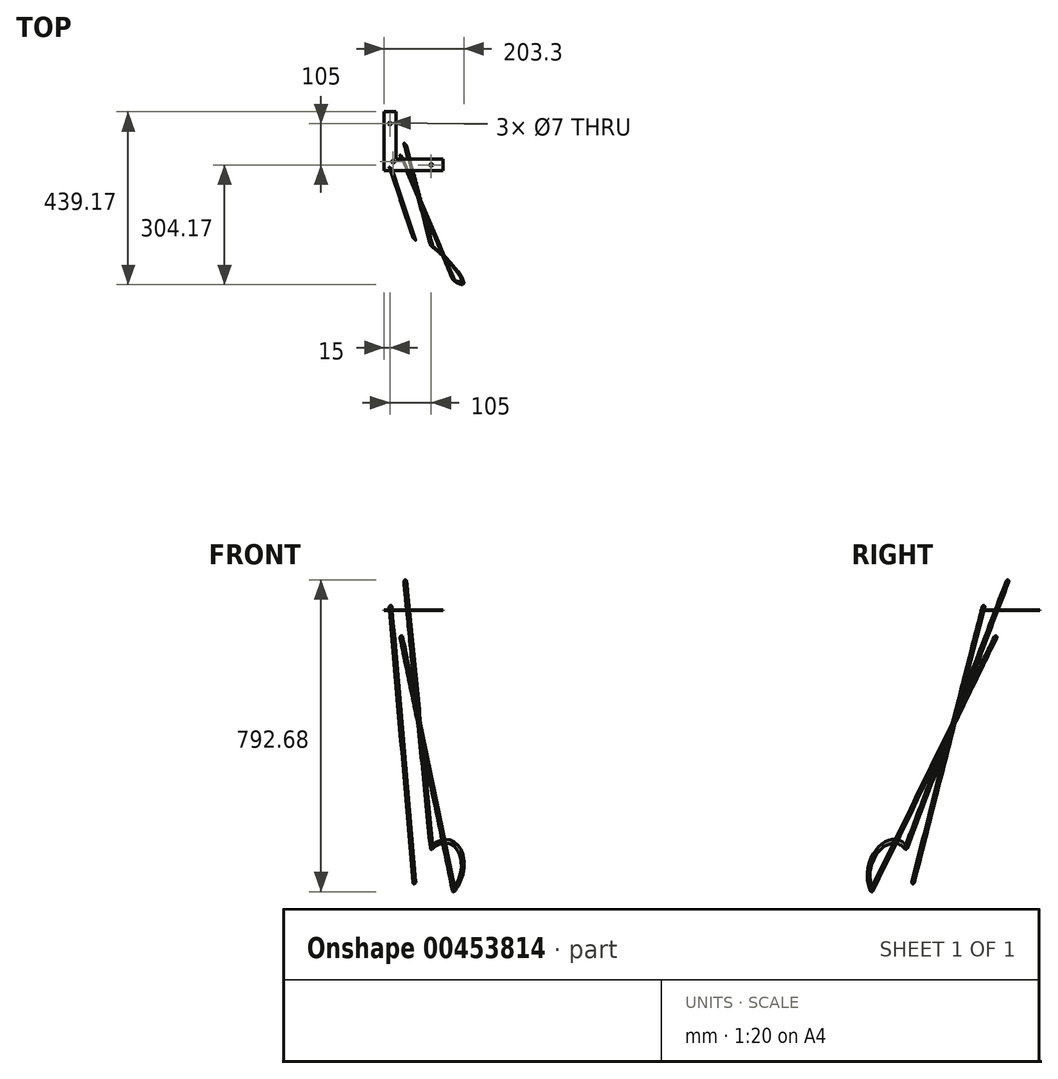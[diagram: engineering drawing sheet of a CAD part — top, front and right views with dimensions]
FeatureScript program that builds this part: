
annotation { "Feature Type Name" : "Feature", "Feature Type Description" : "" }
export const myFeature = defineFeature(function(context is Context, id is Id, definition is map)
    precondition{}
    {
        {
            var Q0;
            Q0=qCreatedBy(makeId("Top.planeOp"),FACE);
            var sketch = newSketch(context, id + "F0", { "sketchPlane" : qUnion([Q0])});
            skLineSegment(sketch, "E0", {"start": v(0, 0) * mm, "end": v(0, 150) * mm});
            skLineSegment(sketch, "E1", {"start": v(0, 150) * mm, "end": v(30, 150) * mm});
            skLineSegment(sketch, "E2", {"start": v(30, 150) * mm, "end": v(30, 30) * mm});
            skLineSegment(sketch, "E3", {"start": v(30, 30) * mm, "end": v(150, 30) * mm});
            skLineSegment(sketch, "E4", {"start": v(150, 30) * mm, "end": v(150, 0) * mm});
            skLineSegment(sketch, "E5", {"start": v(150, 0) * mm, "end": v(0, 0) * mm});
            skLineSegment(sketch, "E6", {"start": v(0, 150) * mm, "end": v(10, 150) * mm});
            skLineSegment(sketch, "E7", {"start": v(10, 150) * mm, "end": v(10, -10.8) * mm, "construction": true});
            skLineSegment(sketch, "E8", {"start": v(150, 0) * mm, "end": v(150, 10) * mm});
            skLineSegment(sketch, "E9", {"start": v(150, 10) * mm, "end": v(-41.67, 10) * mm, "construction": true});
            skCircle(sketch, "E10", {"center": v(10, 10) * mm, "radius": 4.75 * mm});
            skLineSegment(sketch, "E11", {"start": v(150, 10) * mm, "end": v(90, 10) * mm, "construction": true});
            skLineSegment(sketch, "E12", {"start": v(10, 150) * mm, "end": v(10, 90) * mm, "construction": true});
            skCircle(sketch, "E13", {"center": v(10, 90) * mm, "radius": 4.75 * mm});
            skCircle(sketch, "E14", {"center": v(90, 10) * mm, "radius": 4.75 * mm});
            skLineSegment(sketch, "E15", {"start": v(15, 150) * mm, "end": v(15, 120) * mm, "construction": true});
            skLineSegment(sketch, "E16", {"start": v(150, 15) * mm, "end": v(120, 15) * mm, "construction": true});
            skLineSegment(sketch, "E17", {"start": v(30, 30) * mm, "end": v(30, 23) * mm, "construction": true});
            skLineSegment(sketch, "E18", {"start": v(30, 23) * mm, "end": v(23, 23) * mm, "construction": true});
            skCircle(sketch, "E19", {"center": v(23, 23) * mm, "radius": 3.5 * mm});
            skCircle(sketch, "E20", {"center": v(120, 15) * mm, "radius": 3.5 * mm});
            skCircle(sketch, "E21", {"center": v(15, 120) * mm, "radius": 3.5 * mm});
            skLineSegment(sketch, "E22", {"start": v(10, 90) * mm, "end": v(90, 10) * mm, "construction": true});
            skLineSegment(sketch, "E23", {"start": v(10, 10) * mm, "end": v(87.96, -67.96) * mm, "construction": true});
            skSolve(sketch);
        }
        {
            var Q0;
            Q0=qSketchRegion(id+"F0",true);
            var Q1;
            Q1=makeQuery(id+"F0.imprint","IMPRINT",FACE,{"disambiguationData":[TD([[makeQuery(id+"F0.imprint","IMPRINT",EDGE,{"derivedFrom":sQuery(id+"F0.wireOp",EDGE,"E10")}),1.0]])]});
            var Q2;
            Q2=makeQuery(id+"F0.imprint","IMPRINT",FACE,{"disambiguationData":[TD([[makeQuery(id+"F0.imprint","IMPRINT",EDGE,{"derivedFrom":sQuery(id+"F0.wireOp",EDGE,"E14")}),1.0]])]});
            var Q3;
            Q3=makeQuery(id+"F0.imprint","IMPRINT",FACE,{"disambiguationData":[TD([[makeQuery(id+"F0.imprint","IMPRINT",EDGE,{"derivedFrom":sQuery(id+"F0.wireOp",EDGE,"E13")}),1.0]])]});
            extrude(context, id + "F1", {"entities" : qUnion([Q0, Q1, Q2, Q3]), "depth" : 2.5 * mm});
        }
        {
            var Q0;
            Q0=qCreatedBy(makeId("Right.planeOp"),FACE);
            var sketch = newSketch(context, id + "F2", { "sketchPlane" : qUnion([Q0])});
            skLineSegment(sketch, "E24", {"start": v(0, 0) * mm, "end": v(0, -710) * mm});
            skLineSegment(sketch, "E25", {"start": v(0, -710) * mm, "end": v(-50, -710) * mm});
            skSolve(sketch);
        }
        {
            var Q0;
            Q0=qCreatedBy(makeId("Front.planeOp"),FACE);
            var sketch = newSketch(context, id + "F3", { "sketchPlane" : qUnion([Q0])});
            skLineSegment(sketch, "E26", {"start": v(0, 0) * mm, "end": v(0, -710) * mm});
            skLineSegment(sketch, "E27", {"start": v(0, -710) * mm, "end": v(-50, -710) * mm});
            skSolve(sketch);
        }
        {
            var Q0;
            Q0=sQuery(id+"F3.wireOp",VERTEX,"E27.end");
            var Q1;
            Q1=sQuery(id+"F3.wireOp",VERTEX,"E27.start");
            var Q2;
            Q2=sQuery(id+"F2.wireOp",VERTEX,"E25.end");
            cPlane(context, id + "F4", {"entities" : qUnion([Q0, Q1, Q2]), "cplaneType" : CPlaneType.THREE_POINT, "offset" : 150 * mm, "width" : 150 * mm, "height" : 150 * mm});
        }
        {
            var Q0;
            Q0=qCreatedBy(id+"F4.planeOp",FACE);
            var sketch = newSketch(context, id + "F5", { "sketchPlane" : qUnion([Q0])});
            skLineSegment(sketch, "E28.bottom", {"start": v(0, 0) * mm, "end": v(-50, 0) * mm});
            skLineSegment(sketch, "E28.top", {"start": v(0, -50) * mm, "end": v(-50, -50) * mm});
            skLineSegment(sketch, "E28.left", {"start": v(0, 0) * mm, "end": v(0, -50) * mm});
            skLineSegment(sketch, "E28.right", {"start": v(-50, 0) * mm, "end": v(-50, -50) * mm});
            skSolve(sketch);
        }
        {
            var Q0;
            Q0=sQuery(id+"F0.wireOp",VERTEX,"E13.center");
            var Q1;
            Q1=sQuery(id+"F0.wireOp",VERTEX,"E14.center");
            var Q2;
            Q2=sQuery(id+"F5.wireOp",VERTEX,"E28.right.end");
            cPlane(context, id + "F6", {"entities" : qUnion([Q0, Q1, Q2]), "cplaneType" : CPlaneType.THREE_POINT, "offset" : 150 * mm, "width" : 150 * mm, "height" : 150 * mm});
        }
        {
            var Q0;
            Q0=qCreatedBy(id+"F6.planeOp",FACE);
            var sketch = newSketch(context, id + "F7", { "sketchPlane" : qUnion([Q0])});
            skPoint(sketch, "E29", {"position": v(-58.17, 2.71) * mm});
            skPoint(sketch, "E30", {"position": v(52.87, 24.4) * mm});
            skPoint(sketch, "E31", {"position": v(136.15, -696.96) * mm});
            skLineSegment(sketch, "E32", {"start": v(136.15, -696.96) * mm, "end": v(-58.17, 2.71) * mm, "construction": true});
            skLineSegment(sketch, "E33", {"start": v(52.87, 24.4) * mm, "end": v(136.15, -696.96) * mm, "construction": true});
            skLineSegment(sketch, "E34", {"start": v(-58.17, 2.71) * mm, "end": v(52.87, 24.4) * mm, "construction": true});
            skLineSegment(sketch, "E35", {"start": v(-2.65, 13.56) * mm, "end": v(166.07, -850.12) * mm, "construction": true});
            skLineSegment(sketch, "E36", {"start": v(146.1, -695.84) * mm, "end": v(52.87, 24.4) * mm});
            skLineSegment(sketch, "E37", {"start": v(-58.17, 2.71) * mm, "end": v(126.51, -699.67) * mm});
            skPoint(sketch, "E38.visualSharp", {"position": v(166.07, -850.12) * mm});
            skArc(sketch, "E38.filletArc", {"start": v(126.51, -699.67) * mm, "mid": v(138.1, -706.94) * mm, "end": v(146.1, -695.84) * mm});
            skSolve(sketch);
        }
        {
            var Q0;
            Q0=sQuery(id+"F7.wireOp",EDGE,"E34");
            cPlane(context, id + "F8", {"entities" : qUnion([Q0]), "cplaneType" : CPlaneType.LINE_ANGLE, "offset" : 150 * mm, "angle" : 168 * degree, "width" : 150 * mm, "height" : 150 * mm});
        }
        {
            var Q0;
            Q0=qCreatedBy(id+"F8.planeOp",FACE);
            var sketch = newSketch(context, id + "F9", { "sketchPlane" : qUnion([Q0])});
            skPoint(sketch, "E39", {"position": v(7.92, 89) * mm});
            skPoint(sketch, "E40", {"position": v(88.8, 9.89) * mm});
            skCircle(sketch, "E41", {"center": v(7.92, 89) * mm, "radius": 4.75 * mm});
            skSolve(sketch);
        }
        {
            var Q0;
            Q0=qSketchRegion(id+"F9",true);
            var Q1;
            Q1=sQuery(id+"F9.wireOp",EDGE,"E41");
            var Q2;
            Q2=sQuery(id+"F7.wireOp",EDGE,"E37");
            var Q3;
            Q3=sQuery(id+"F7.wireOp",EDGE,"E38.filletArc");
            var Q4;
            Q4=sQuery(id+"F7.wireOp",EDGE,"E36");
            sweep(context, id + "F10", {"profiles" : qUnion([Q0]), "surfaceProfiles" : qUnion([Q1]), "path" : qUnion([Q2, Q3, Q4])});
        }
        {
            var Q0;
            Q0=sQuery(id+"F0.wireOp",EDGE,"E23");
            var Q1;
            Q1=sQuery(id+"F5.wireOp",VERTEX,"E28.right.end");
            cPlane(context, id + "F11", {"entities" : qUnion([Q0, Q1]), "cplaneType" : CPlaneType.LINE_POINT, "offset" : 150 * mm, "width" : 150 * mm, "height" : 150 * mm});
        }
        {
            var Q0;
            Q0=sQuery(id+"F0.wireOp",VERTEX,"E23.start");
            var Q1;
            Q1=sQuery(id+"F0.wireOp",VERTEX,"E23.end");
            var Q2;
            Q2=sQuery(id+"F5.wireOp",VERTEX,"E28.right.end");
            cPlane(context, id + "F12", {"entities" : qUnion([Q0, Q1, Q2]), "cplaneType" : CPlaneType.THREE_POINT, "offset" : 150 * mm, "width" : 150 * mm, "height" : 150 * mm});
        }
        {
            var Q0;
            Q0=qCreatedBy(id+"F12.planeOp",FACE);
            var sketch = newSketch(context, id + "F13", { "sketchPlane" : qUnion([Q0])});
            skPoint(sketch, "E42", {"position": v(84.06, -708.4) * mm});
            skPoint(sketch, "E43", {"position": v(-0.2, 1.67) * mm});
            skLineSegment(sketch, "E44", {"start": v(-0.2, 1.67) * mm, "end": v(84.06, -708.4) * mm, "construction": true});
            skLineSegment(sketch, "E45", {"start": v(81.03, -682.82) * mm, "end": v(84.99, -716.2) * mm, "construction": true});
            skLineSegment(sketch, "E46", {"start": v(84.99, -716.2) * mm, "end": v(-0.2, 1.67) * mm});
            skSolve(sketch);
        }
        {
            var Q0;
            Q0=qCreatedBy(id+"F8.planeOp",FACE);
            var Q1;
            Q1=sQuery(id+"F13.wireOp",VERTEX,"E43");
            cPlane(context, id + "F14", {"entities" : qUnion([Q0, Q1]), "cplaneType" : CPlaneType.PLANE_POINT, "offset" : 150 * mm, "width" : 150 * mm, "height" : 150 * mm});
        }
        {
            var Q0;
            Q0=qCreatedBy(id+"F14.planeOp",FACE);
            var sketch = newSketch(context, id + "F15", { "sketchPlane" : qUnion([Q0])});
            skPoint(sketch, "E47", {"position": v(9.67, 9.89) * mm});
            skCircle(sketch, "E48", {"center": v(9.67, 9.89) * mm, "radius": 4.75 * mm});
            skSolve(sketch);
        }
        {
            var Q0;
            Q0=qSketchRegion(id+"F15",true);
            var Q1;
            Q1=qConstructionFilter(qBodyType(qCreatedBy(id+"F13",EDGE),BodyType.WIRE),ConstructionObject.NO);
            sweep(context, id + "F16", {"operationType" : NewBodyOperationType.ADD, "profiles" : qUnion([Q0]), "path" : qUnion([Q1])});
        }
    });
